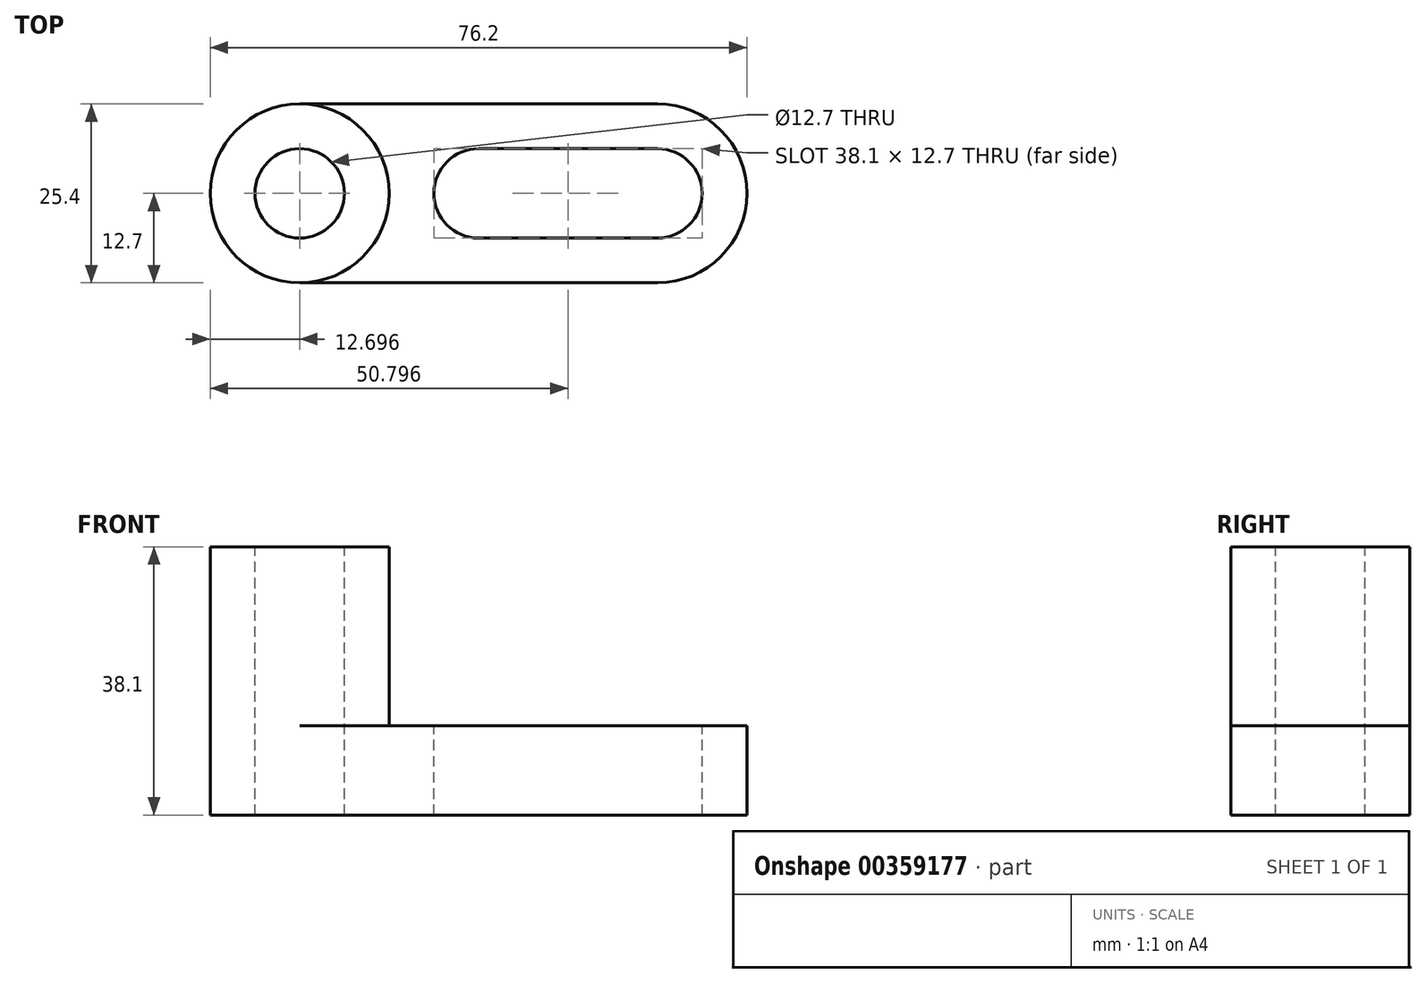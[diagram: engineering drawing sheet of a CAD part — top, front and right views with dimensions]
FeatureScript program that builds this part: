
annotation { "Feature Type Name" : "Feature", "Feature Type Description" : "" }
export const myFeature = defineFeature(function(context is Context, id is Id, definition is map)
    precondition{}
    {
        {
            var Q0;
            Q0=qCreatedBy(makeId("Front.planeOp"),FACE);
            var sketch = newSketch(context, id + "F0", { "sketchPlane" : qUnion([Q0])});
            skLineSegment(sketch, "E0", {"start": v(-33.58, 25.4) * mm, "end": v(-33.58, -12.7) * mm});
            skLineSegment(sketch, "E1", {"start": v(-33.58, -12.7) * mm, "end": v(42.62, -12.7) * mm});
            skLineSegment(sketch, "E2", {"start": v(42.62, -12.7) * mm, "end": v(42.62, 0) * mm});
            skLineSegment(sketch, "E3", {"start": v(42.62, 0) * mm, "end": v(-8.18, 0) * mm});
            skLineSegment(sketch, "E4", {"start": v(-8.18, 0) * mm, "end": v(-8.18, 25.4) * mm});
            skLineSegment(sketch, "E5", {"start": v(-8.18, 25.4) * mm, "end": v(-33.58, 25.4) * mm});
            skSolve(sketch);
        }
        {
            var Q0;
            Q0 = qSketchRegion(id + "F0", true);
            extrude(context, id + "F1", {"entities" : qUnion([Q0]), "depth" : 25.4 * mm});
        }
        {
            var Q0;
            Q0=makeQuery(id+"F1.opExtrude","SWEPT_FACE",FACE,{"disambiguationData":[OSD([sQuery(id+"F0.wireOp",EDGE,"E3")])]});
            var sketch = newSketch(context, id + "F2", { "sketchPlane" : qUnion([Q0])});
            skLineSegment(sketch, "E6", {"start": v(29.85, 0) * mm, "end": v(29.92, 0) * mm});
            skLineSegment(sketch, "E7", {"start": v(42.62, -12.7) * mm, "end": v(42.62, -12.7) * mm});
            skLineSegment(sketch, "E8", {"start": v(29.92, -25.4) * mm, "end": v(28.83, -25.4) * mm});
            skPoint(sketch, "E9.visualSharp", {"position": v(42.62, 0) * mm});
            skArc(sketch, "E9.filletArc", {"start": v(42.62, -12.7) * mm, "mid": v(38.9, -3.72) * mm, "end": v(29.92, 0) * mm});
            skPoint(sketch, "E10.visualSharp", {"position": v(42.62, -25.4) * mm});
            skArc(sketch, "E10.filletArc", {"start": v(29.92, -25.4) * mm, "mid": v(38.9, -21.68) * mm, "end": v(42.62, -12.7) * mm});
            skCircle(sketch, "E11", {"center": v(29.92, -12.7) * mm, "radius": 6.35 * mm});
            skCircle(sketch, "E12", {"center": v(4.52, -12.7) * mm, "radius": 6.35 * mm});
            skLineSegment(sketch, "E13", {"start": v(4.52, -6.35) * mm, "end": v(29.92, -6.35) * mm});
            skLineSegment(sketch, "E14", {"start": v(4.52, -19.05) * mm, "end": v(29.92, -19.05) * mm});
            skSolve(sketch);
        }
        {
            var Q0;
            Q0 = qSketchRegion(id + "F2", true);
            var Q1;
            {var subQ0=sQuery(id+"F2.wireOp",EDGE,"E9.filletArc");Q1=makeQuery(id+"F2.imprint","IMPRINT",FACE,{"disambiguationData":[TD([[makeQuery(id+"F2.imprint","IMPRINT",EDGE,{"derivedFrom":subQ0}),-1.0]])]});}
            var Q2;
            {var subQ0=sQuery(id+"F2.wireOp",EDGE,"E10.filletArc");Q2=makeQuery(id+"F2.imprint","IMPRINT",FACE,{"disambiguationData":[TD([[makeQuery(id+"F2.imprint","IMPRINT",EDGE,{"derivedFrom":subQ0}),-1.0]])]});}
            extrude(context, id + "F3", {"entities" : qUnion([Q0, Q1, Q2]), "operationType" : NewBodyOperationType.REMOVE, "oppositeDirection" : true, "depth" : 25.4 * mm});
        }
        {
            var Q0;
            Q0=makeQuery(id+"F1.opExtrude","SWEPT_FACE",FACE,{"disambiguationData":[OSD([sQuery(id+"F0.wireOp",EDGE,"E5")])]});
            var sketch = newSketch(context, id + "F4", { "sketchPlane" : qUnion([Q0])});
            skLineSegment(sketch, "E15", {"start": v(-20.88, 0) * mm, "end": v(-20.88, 0) * mm});
            skLineSegment(sketch, "E16", {"start": v(-8.18, -12.7) * mm, "end": v(-8.18, -12.7) * mm});
            skLineSegment(sketch, "E17", {"start": v(-20.88, -25.4) * mm, "end": v(-20.88, -25.4) * mm});
            skLineSegment(sketch, "E18", {"start": v(-33.58, -12.7) * mm, "end": v(-33.58, -12.7) * mm});
            skPoint(sketch, "E19.visualSharp", {"position": v(-33.58, 0) * mm});
            skArc(sketch, "E19.filletArc", {"start": v(-20.88, 0) * mm, "mid": v(-29.86, -3.72) * mm, "end": v(-33.58, -12.7) * mm});
            skPoint(sketch, "E20.visualSharp", {"position": v(-8.18, 0) * mm});
            skArc(sketch, "E20.filletArc", {"start": v(-8.18, -12.7) * mm, "mid": v(-11.9, -3.72) * mm, "end": v(-20.88, 0) * mm});
            skPoint(sketch, "E21.visualSharp", {"position": v(-8.18, -25.4) * mm});
            skArc(sketch, "E21.filletArc", {"start": v(-20.88, -25.4) * mm, "mid": v(-11.9, -21.68) * mm, "end": v(-8.18, -12.7) * mm});
            skPoint(sketch, "E22.visualSharp", {"position": v(-33.58, -25.4) * mm});
            skArc(sketch, "E22.filletArc", {"start": v(-33.58, -12.7) * mm, "mid": v(-29.86, -21.68) * mm, "end": v(-20.88, -25.4) * mm});
            skCircle(sketch, "E23", {"center": v(-20.88, -12.7) * mm, "radius": 6.35 * mm});
            skSolve(sketch);
        }
        {
            var Q0;
            Q0=makeQuery(id+"F4.imprint","IMPRINT",FACE,{"disambiguationData":[TD([[makeQuery(id+"F4.imprint","IMPRINT",EDGE,{"derivedFrom":sQuery(id+"F4.wireOp",EDGE,"E23")}),1.0]])]});
            var Q1;
            {var subQ0=sQuery(id+"F4.wireOp",EDGE,"E19.filletArc");Q1=makeQuery(id+"F4.imprint","IMPRINT",FACE,{"disambiguationData":[TD([[makeQuery(id+"F4.imprint","IMPRINT",EDGE,{"derivedFrom":subQ0}),-1.0]])]});}
            var Q2;
            {var subQ0=sQuery(id+"F4.wireOp",EDGE,"E22.filletArc");Q2=makeQuery(id+"F4.imprint","IMPRINT",FACE,{"disambiguationData":[TD([[makeQuery(id+"F4.imprint","IMPRINT",EDGE,{"derivedFrom":subQ0}),-1.0]])]});}
            extrude(context, id + "F5", {"entities" : qUnion([Q0, Q1, Q2]), "operationType" : NewBodyOperationType.REMOVE, "oppositeDirection" : true, "depth" : 38.1 * mm});
        }
        {
            var Q0;
            Q0=makeQuery(id+"F1.opExtrude","SWEPT_FACE",FACE,{"disambiguationData":[OSD([sQuery(id+"F0.wireOp",EDGE,"E5")])]});
            var sketch = newSketch(context, id + "F6", { "sketchPlane" : qUnion([Q0])});
            skLineSegment(sketch, "E24", {"start": v(-20.88, 0) * mm, "end": v(-17.64, 0) * mm});
            skLineSegment(sketch, "E25", {"start": v(-8.18, -12.7) * mm, "end": v(-8.18, -12.7) * mm});
            skLineSegment(sketch, "E26", {"start": v(-18.57, -25.4) * mm, "end": v(-20.88, -25.4) * mm});
            skPoint(sketch, "E27.visualSharp", {"position": v(-8.18, 0) * mm});
            skArc(sketch, "E27.filletArc", {"start": v(-8.18, -12.7) * mm, "mid": v(-11.9, -3.72) * mm, "end": v(-20.88, 0) * mm});
            skPoint(sketch, "E28.visualSharp", {"position": v(-8.18, -25.4) * mm});
            skArc(sketch, "E28.filletArc", {"start": v(-20.88, -25.4) * mm, "mid": v(-11.9, -21.68) * mm, "end": v(-8.18, -12.7) * mm});
            skSolve(sketch);
        }
        {
            var Q0;
            Q0 = qSketchRegion(id + "F6", true);
            var Q1;
            {var subQ0=sQuery(id+"F6.wireOp",EDGE,"E24");Q1=makeQuery(id+"F6.imprint","IMPRINT",FACE,{"disambiguationData":[TD([[makeQuery(id+"F6.imprint","IMPRINT",EDGE,{"derivedFrom":subQ0}),1.0]])]});}
            var Q2;
            {var subQ0=sQuery(id+"F6.wireOp",EDGE,"E26");Q2=makeQuery(id+"F6.imprint","IMPRINT",FACE,{"disambiguationData":[TD([[makeQuery(id+"F6.imprint","IMPRINT",EDGE,{"derivedFrom":subQ0}),-1.0]])]});}
            extrude(context, id + "F7", {"entities" : qUnion([Q0, Q1, Q2]), "operationType" : NewBodyOperationType.REMOVE, "oppositeDirection" : true, "depth" : 25.4 * mm});
        }
    });
